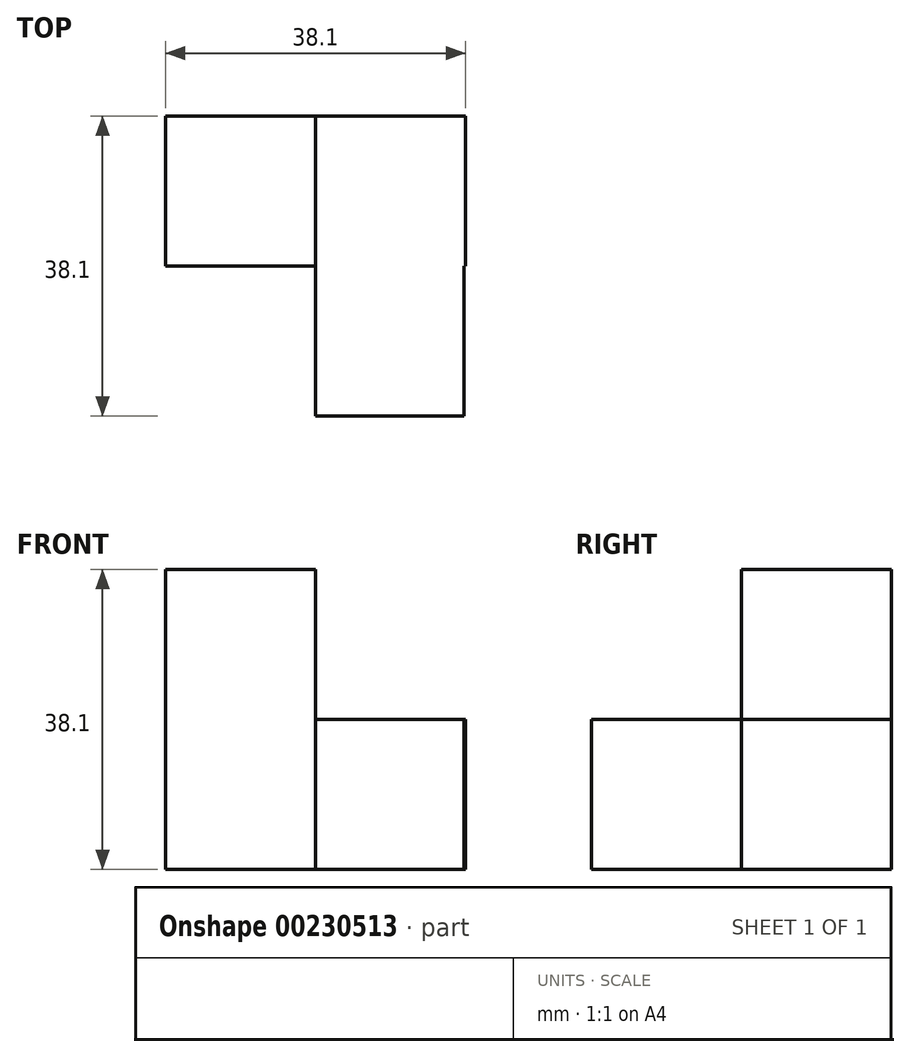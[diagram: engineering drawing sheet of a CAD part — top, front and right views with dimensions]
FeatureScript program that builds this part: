
annotation { "Feature Type Name" : "Feature", "Feature Type Description" : "" }
export const myFeature = defineFeature(function(context is Context, id is Id, definition is map)
    precondition{}
    {
        {
            var Q0;
            Q0=qCreatedBy(makeId("Top.planeOp"),FACE);
            var sketch = newSketch(context, id + "F0", { "sketchPlane" : qUnion([Q0])});
            skLineSegment(sketch, "E0.bottom", {"start": v(-37.9, -22.56) * mm, "end": v(-18.85, -22.56) * mm});
            skLineSegment(sketch, "E0.top", {"start": v(-37.9, -3.5) * mm, "end": v(-18.85, -3.5) * mm});
            skLineSegment(sketch, "E0.left", {"start": v(-37.9, -22.56) * mm, "end": v(-37.9, -3.5) * mm});
            skLineSegment(sketch, "E0.right", {"start": v(-18.85, -22.56) * mm, "end": v(-18.85, -3.5) * mm});
            skSolve(sketch);
        }
        {
            var Q0;
            Q0=makeQuery(id+"F0.imprint","IMPRINT",FACE,{"disambiguationData":[TD([[makeQuery(id+"F0.imprint","IMPRINT",EDGE,{"derivedFrom":sQuery(id+"F0.wireOp",EDGE,"E0.bottom")}),1.0]])]});
            extrude(context, id + "F1", {"entities" : qUnion([Q0]), "depth" : 38.1 * mm});
        }
        {
            var Q0;
            Q0=makeQuery(id+"F1.opExtrude","SWEPT_FACE",FACE,{"disambiguationData":[OSD([sQuery(id+"F0.wireOp",EDGE,"E0.right")])]});
            var sketch = newSketch(context, id + "F2", { "sketchPlane" : qUnion([Q0])});
            skLineSegment(sketch, "E1.bottom", {"start": v(-22.56, 0) * mm, "end": v(-3.5, 0) * mm});
            skLineSegment(sketch, "E1.top", {"start": v(-22.56, 19.05) * mm, "end": v(-3.5, 19.05) * mm});
            skLineSegment(sketch, "E1.left", {"start": v(-22.56, 0) * mm, "end": v(-22.56, 19.05) * mm});
            skLineSegment(sketch, "E1.right", {"start": v(-3.5, 0) * mm, "end": v(-3.5, 19.05) * mm});
            skSolve(sketch);
        }
        {
            var Q0;
            Q0=makeQuery(id+"F2.imprint","IMPRINT",FACE,{"disambiguationData":[TD([[makeQuery(id+"F2.imprint","IMPRINT",EDGE,{"derivedFrom":sQuery(id+"F2.wireOp",EDGE,"E1.bottom")}),1.0]])]});
            extrude(context, id + "F3", {"entities" : qUnion([Q0]), "operationType" : NewBodyOperationType.ADD, "depth" : 19.05 * mm});
        }
        {
            var Q0;
            Q0=makeQuery(id+"F3.boolean.opBoolean","MERGE",FACE,{"derivedFrom":[makeQuery(id+"F1.opExtrude","SWEPT_FACE",FACE,{"disambiguationData":[OSD([sQuery(id+"F0.wireOp",EDGE,"E0.bottom")])]}),makeQuery(id+"F3.opExtrude","SWEPT_FACE",FACE,{"disambiguationData":[OSD([sQuery(id+"F2.wireOp",EDGE,"E1.left")])]})]});
            var sketch = newSketch(context, id + "F4", { "sketchPlane" : qUnion([Q0])});
            skLineSegment(sketch, "E2.bottom", {"start": v(-18.85, 19.05) * mm, "end": v(0, 19.05) * mm});
            skLineSegment(sketch, "E2.top", {"start": v(-18.85, 0) * mm, "end": v(0, 0) * mm});
            skLineSegment(sketch, "E2.left", {"start": v(-18.85, 19.05) * mm, "end": v(-18.85, 0) * mm});
            skLineSegment(sketch, "E2.right", {"start": v(0, 19.05) * mm, "end": v(0, 0) * mm});
            skSolve(sketch);
        }
        {
            var Q0;
            Q0=makeQuery(id+"F4.imprint","IMPRINT",FACE,{"disambiguationData":[TD([[makeQuery(id+"F4.imprint","IMPRINT",EDGE,{"derivedFrom":sQuery(id+"F4.wireOp",EDGE,"E2.bottom")}),1.0]])]});
            extrude(context, id + "F5", {"entities" : qUnion([Q0]), "operationType" : NewBodyOperationType.ADD, "depth" : 19.05 * mm});
        }
    });
